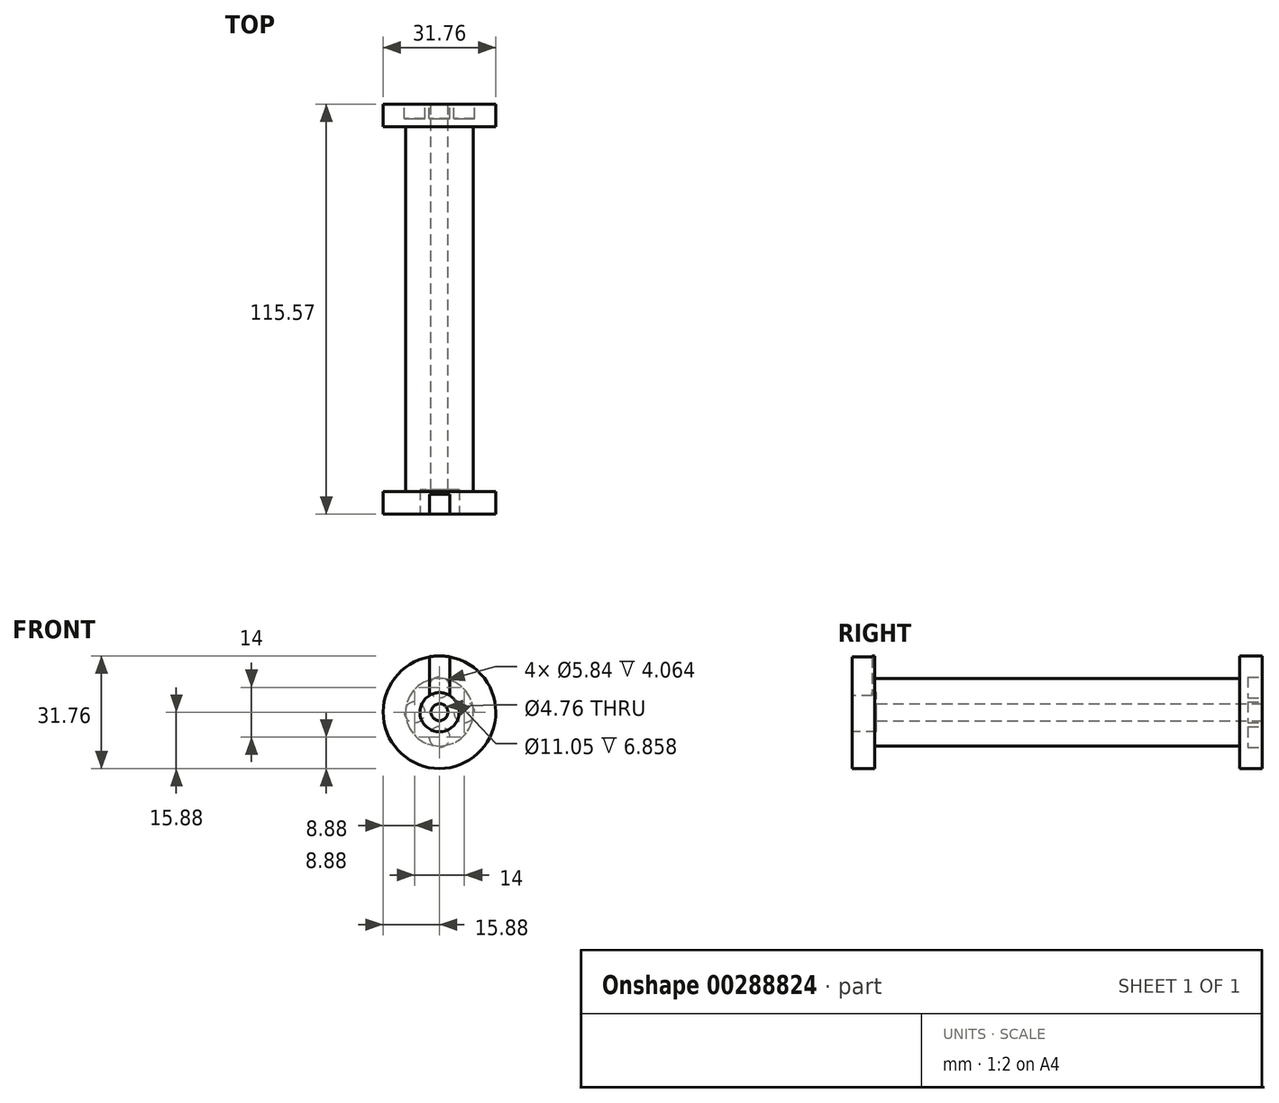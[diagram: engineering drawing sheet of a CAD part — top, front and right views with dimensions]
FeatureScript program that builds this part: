
annotation { "Feature Type Name" : "Feature", "Feature Type Description" : "" }
export const myFeature = defineFeature(function(context is Context, id is Id, definition is map)
    precondition{}
    {
        {
            var Q0;
            Q0=qCreatedBy(makeId("Front.planeOp"),FACE);
            var sketch = newSketch(context, id + "F0", { "sketchPlane" : qUnion([Q0])});
            skCircle(sketch, "E0", {"center": v(0, 0) * mm, "radius": 9.52 * mm});
            skCircle(sketch, "E1", {"center": v(0, 0) * mm, "radius": 2.38 * mm});
            skSolve(sketch);
        }
        {
            var Q0;
            Q0=makeQuery(id+"F0.imprint","IMPRINT",FACE,{"disambiguationData":[TD([[makeQuery(id+"F0.imprint","IMPRINT",EDGE,{"derivedFrom":sQuery(id+"F0.wireOp",EDGE,"E0")}),1.0]])]});
            extrude(context, id + "F1", {"entities" : qUnion([Q0]), "depth" : 115.57 * mm});
        }
        {
            var Q0;
            Q0=makeQuery(id+"F1.opExtrude","CAP_FACE",FACE,{"disambiguationData":[OSD([sQuery(id+"F0.wireOp",EDGE,"E0"),sQuery(id+"F0.wireOp",EDGE,"E1")])],"isStart":true});
            var sketch = newSketch(context, id + "F2", { "sketchPlane" : qUnion([Q0])});
            skCircle(sketch, "E2", {"center": v(0, 0) * mm, "radius": 15.88 * mm});
            skSolve(sketch);
        }
        {
            var Q0;
            Q0=makeQuery(id+"F2.imprint","IMPRINT",FACE,{"disambiguationData":[TD([[makeQuery(id+"F2.imprint","IMPRINT",EDGE,{"derivedFrom":sQuery(id+"F2.wireOp",EDGE,"E2")}),1.0]])]});
            extrude(context, id + "F3", {"entities" : qUnion([Q0]), "operationType" : NewBodyOperationType.ADD, "oppositeDirection" : true, "depth" : 6.35 * mm});
        }
        {
            var Q0;
            {var subQ0=sQuery(id+"F0.wireOp",EDGE,"E0");Q0=makeQuery(id+"F3.boolean.opBoolean","MERGE",FACE,{"derivedFrom":[makeQuery(id+"F1.opExtrude","CAP_FACE",FACE,{"disambiguationData":[OSD([subQ0,sQuery(id+"F0.wireOp",EDGE,"E1")])],"isStart":true}),makeQuery(id+"F3.opExtrude","CAP_FACE",FACE,{"disambiguationData":[OSD([subQ0,sQuery(id+"F2.wireOp",EDGE,"E2")])],"isStart":true})]});}
            var sketch = newSketch(context, id + "F4", { "sketchPlane" : qUnion([Q0])});
            skLineSegment(sketch, "E3", {"start": v(0, 0) * mm, "end": v(0, 7) * mm});
            skLineSegment(sketch, "E4", {"start": v(0, 7) * mm, "end": v(0, -7) * mm});
            skLineSegment(sketch, "E5", {"start": v(0, 0) * mm, "end": v(7, 0) * mm});
            skLineSegment(sketch, "E6", {"start": v(0, 0) * mm, "end": v(-7, 0) * mm});
            skLineSegment(sketch, "E7", {"start": v(-7, 0) * mm, "end": v(7, 0) * mm});
            skCircle(sketch, "E8", {"center": v(-7, 0) * mm, "radius": 2.92 * mm});
            skCircle(sketch, "E9", {"center": v(7, 0) * mm, "radius": 2.92 * mm});
            skCircle(sketch, "E10", {"center": v(0, -7) * mm, "radius": 2.92 * mm});
            skCircle(sketch, "E11", {"center": v(0, 7) * mm, "radius": 2.92 * mm});
            skSolve(sketch);
        }
        {
            var Q0;
            Q0=makeQuery(id+"F4.imprint","IMPRINT",FACE,{"disambiguationData":[TD([[makeQuery(id+"F4.imprint","IMPRINT",EDGE,{"derivedFrom":sQuery(id+"F4.wireOp",EDGE,"E11")}),1.0]])]});
            var Q1;
            Q1=makeQuery(id+"F4.imprint","IMPRINT",FACE,{"disambiguationData":[TD([[makeQuery(id+"F4.imprint","IMPRINT",EDGE,{"derivedFrom":sQuery(id+"F4.wireOp",EDGE,"E8")}),1.0]])]});
            var Q2;
            Q2=makeQuery(id+"F4.imprint","IMPRINT",FACE,{"disambiguationData":[TD([[makeQuery(id+"F4.imprint","IMPRINT",EDGE,{"derivedFrom":sQuery(id+"F4.wireOp",EDGE,"E10")}),1.0]])]});
            var Q3;
            Q3=makeQuery(id+"F4.imprint","IMPRINT",FACE,{"disambiguationData":[TD([[makeQuery(id+"F4.imprint","IMPRINT",EDGE,{"derivedFrom":sQuery(id+"F4.wireOp",EDGE,"E9")}),1.0]])]});
            extrude(context, id + "F5", {"entities" : qUnion([Q0, Q1, Q2, Q3]), "operationType" : NewBodyOperationType.REMOVE, "oppositeDirection" : true, "depth" : 4.06 * mm});
        }
        {
            var Q0;
            Q0=makeQuery(id+"F1.opExtrude","CAP_FACE",FACE,{"disambiguationData":[OSD([sQuery(id+"F0.wireOp",EDGE,"E0"),sQuery(id+"F0.wireOp",EDGE,"E1")])],"isStart":false});
            var sketch = newSketch(context, id + "F6", { "sketchPlane" : qUnion([Q0])});
            skCircle(sketch, "E12", {"center": v(0, 0) * mm, "radius": 15.88 * mm});
            skSolve(sketch);
        }
        {
            var Q0;
            Q0=makeQuery(id+"F6.imprint","IMPRINT",FACE,{"disambiguationData":[TD([[makeQuery(id+"F6.imprint","IMPRINT",EDGE,{"derivedFrom":sQuery(id+"F6.wireOp",EDGE,"E12")}),1.0]])]});
            extrude(context, id + "F7", {"entities" : qUnion([Q0]), "operationType" : NewBodyOperationType.ADD, "oppositeDirection" : true, "depth" : 6.35 * mm});
        }
        {
            var Q0;
            Q0=qCreatedBy(makeId("Top.planeOp"),FACE);
            var sketch = newSketch(context, id + "F8", { "sketchPlane" : qUnion([Q0])});
            skLineSegment(sketch, "E13.bottom", {"start": v(2.86, -115.81) * mm, "end": v(-2.86, -115.81) * mm});
            skLineSegment(sketch, "E13.top", {"start": v(2.86, -109.97) * mm, "end": v(-2.86, -109.97) * mm});
            skLineSegment(sketch, "E13.left", {"start": v(2.86, -115.81) * mm, "end": v(2.86, -109.97) * mm});
            skLineSegment(sketch, "E13.right", {"start": v(-2.86, -115.81) * mm, "end": v(-2.86, -109.97) * mm});
            skPoint(sketch, "E13.middle", {"position": v(0, -112.89) * mm});
            skSolve(sketch);
        }
        {
            var Q0;
            Q0=makeQuery(id+"F8.imprint","IMPRINT",FACE,{"disambiguationData":[TD([[makeQuery(id+"F8.imprint","IMPRINT",EDGE,{"derivedFrom":sQuery(id+"F8.wireOp",EDGE,"E13.bottom")}),-1.0]])]});
            extrude(context, id + "F9", {"entities" : qUnion([Q0]), "operationType" : NewBodyOperationType.REMOVE, "depth" : 34.5 * mm});
        }
        {
            var Q0;
            {var subQ0=sQuery(id+"F0.wireOp",EDGE,"E0");Q0=makeQuery(id+"F7.boolean.opBoolean","MERGE",FACE,{"derivedFrom":[makeQuery(id+"F1.opExtrude","CAP_FACE",FACE,{"disambiguationData":[OSD([subQ0,sQuery(id+"F0.wireOp",EDGE,"E1")])],"isStart":false}),makeQuery(id+"F7.opExtrude","CAP_FACE",FACE,{"disambiguationData":[OSD([subQ0,sQuery(id+"F6.wireOp",EDGE,"E12")])],"isStart":true})]});}
            var sketch = newSketch(context, id + "F10", { "sketchPlane" : qUnion([Q0])});
            skCircle(sketch, "E14", {"center": v(0, 0) * mm, "radius": 5.52 * mm});
            skSolve(sketch);
        }
        {
            var Q0;
            Q0=makeQuery(id+"F10.imprint","IMPRINT",FACE,{"disambiguationData":[TD([[makeQuery(id+"F10.imprint","IMPRINT",EDGE,{"derivedFrom":sQuery(id+"F10.wireOp",EDGE,"E14")}),1.0]])]});
            extrude(context, id + "F11", {"entities" : qUnion([Q0]), "operationType" : NewBodyOperationType.REMOVE, "oppositeDirection" : true, "depth" : 6.86 * mm});
        }
    });
